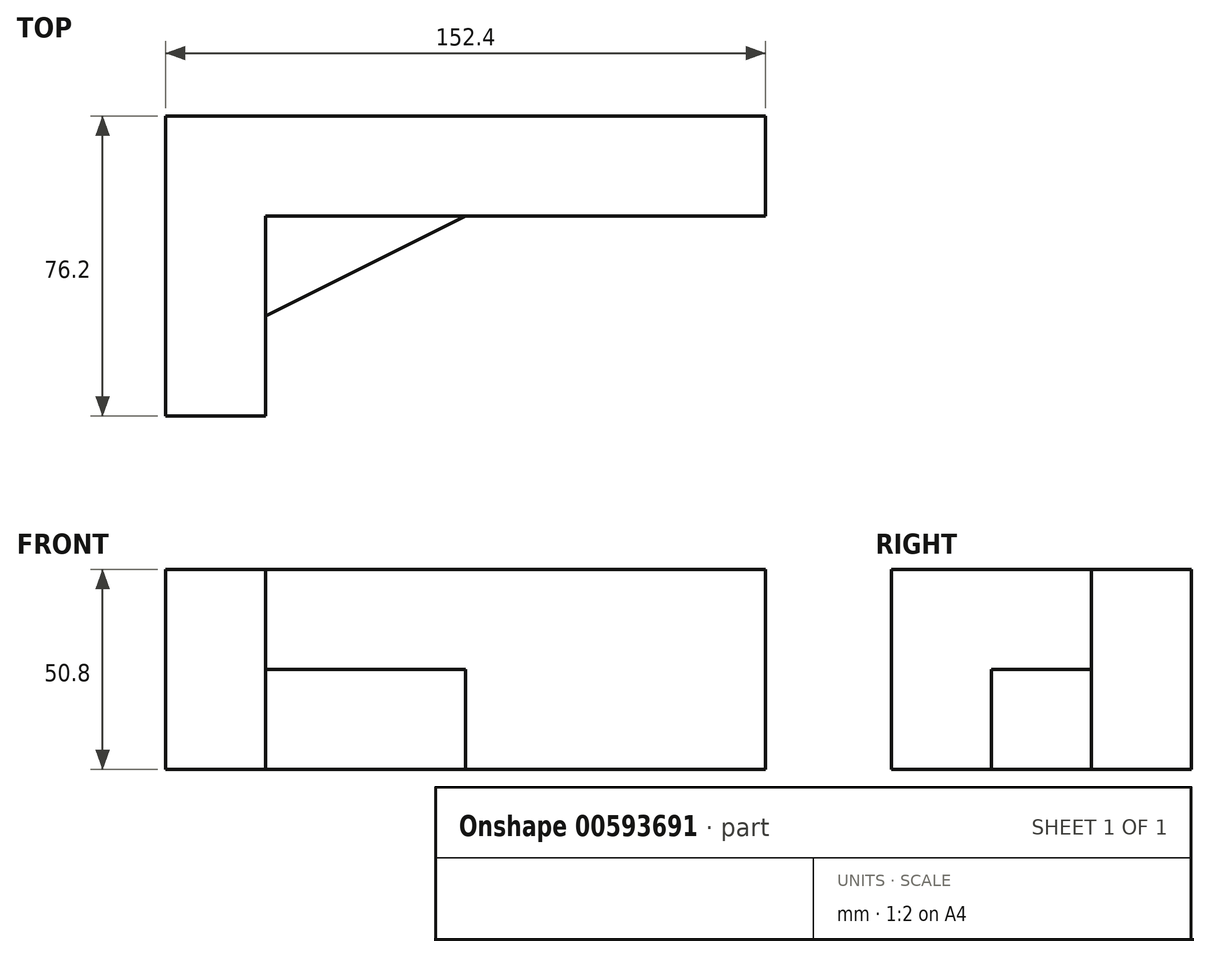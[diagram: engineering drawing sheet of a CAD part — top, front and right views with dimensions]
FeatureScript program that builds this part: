
annotation { "Feature Type Name" : "Feature", "Feature Type Description" : "" }
export const myFeature = defineFeature(function(context is Context, id is Id, definition is map)
    precondition{}
    {
        {
            var Q0;
            Q0=qCreatedBy(makeId("Front.planeOp"),FACE);
            var sketch = newSketch(context, id + "F0", { "sketchPlane" : qUnion([Q0])});
            skLineSegment(sketch, "E0", {"start": v(0, 0) * mm, "end": v(152.4, 0) * mm});
            skLineSegment(sketch, "E1", {"start": v(152.4, 0) * mm, "end": v(152.4, 50.8) * mm});
            skLineSegment(sketch, "E2", {"start": v(152.4, 50.8) * mm, "end": v(0, 50.8) * mm});
            skLineSegment(sketch, "E3", {"start": v(0, 50.8) * mm, "end": v(0, 0) * mm});
            skSolve(sketch);
        }
        {
            var Q0;
            Q0=makeQuery(id+"F0.imprint","IMPRINT",FACE,{"disambiguationData":[TD([[makeQuery(id+"F0.imprint","IMPRINT",EDGE,{"derivedFrom":sQuery(id+"F0.wireOp",EDGE,"E0")}),1.0]])]});
            extrude(context, id + "F1", {"entities" : qUnion([Q0]), "oppositeDirection" : true, "depth" : 76.2 * mm, "offsetDistance" : 25.4 * mm});
        }
        {
            var Q0;
            Q0=makeQuery(id+"F1.opExtrude","CAP_FACE",FACE,{"disambiguationData":[OSD([sQuery(id+"F0.wireOp",EDGE,"E0"),sQuery(id+"F0.wireOp",EDGE,"E1"),sQuery(id+"F0.wireOp",EDGE,"E2"),sQuery(id+"F0.wireOp",EDGE,"E3")])],"isStart":true});
            var sketch = newSketch(context, id + "F2", { "sketchPlane" : qUnion([Q0])});
            skLineSegment(sketch, "E4.bottom", {"start": v(152.4, 0) * mm, "end": v(25.4, 0) * mm});
            skLineSegment(sketch, "E4.top", {"start": v(152.4, 50.8) * mm, "end": v(25.4, 50.8) * mm});
            skLineSegment(sketch, "E4.left", {"start": v(152.4, 0) * mm, "end": v(152.4, 50.8) * mm});
            skLineSegment(sketch, "E4.right", {"start": v(25.4, 0) * mm, "end": v(25.4, 50.8) * mm});
            skSolve(sketch);
        }
        {
            var Q0;
            Q0=makeQuery(id+"F2.imprint","IMPRINT",FACE,{"disambiguationData":[TD([[makeQuery(id+"F2.imprint","IMPRINT",EDGE,{"derivedFrom":sQuery(id+"F2.wireOp",EDGE,"E4.bottom")}),1.0]])]});
            extrude(context, id + "F3", {"entities" : qUnion([Q0]), "operationType" : NewBodyOperationType.REMOVE, "oppositeDirection" : true, "depth" : 50.8 * mm, "offsetDistance" : 25.4 * mm});
        }
        {
            var Q0;
            Q0=makeQuery(id+"F3.boolean.opBoolean","COPY",FACE,{"derivedFrom":makeQuery(id+"F3.opExtrude","CAP_FACE",FACE,{"disambiguationData":[OSD([sQuery(id+"F2.wireOp",EDGE,"E4.bottom"),sQuery(id+"F2.wireOp",EDGE,"E4.top"),sQuery(id+"F2.wireOp",EDGE,"E4.left"),sQuery(id+"F2.wireOp",EDGE,"E4.right")])],"isStart":false})});
            var sketch = newSketch(context, id + "F4", { "sketchPlane" : qUnion([Q0])});
            skLineSegment(sketch, "E5.bottom", {"start": v(25.4, 0) * mm, "end": v(76.2, 0) * mm});
            skLineSegment(sketch, "E5.top", {"start": v(25.4, 25.4) * mm, "end": v(76.2, 25.4) * mm});
            skLineSegment(sketch, "E5.left", {"start": v(25.4, 0) * mm, "end": v(25.4, 25.4) * mm});
            skLineSegment(sketch, "E5.right", {"start": v(76.2, 0) * mm, "end": v(76.2, 25.4) * mm});
            skSolve(sketch);
        }
        {
            var Q0;
            Q0=makeQuery(id+"F4.imprint","IMPRINT",FACE,{"disambiguationData":[TD([[makeQuery(id+"F4.imprint","IMPRINT",EDGE,{"derivedFrom":sQuery(id+"F4.wireOp",EDGE,"E5.bottom")}),1.0]])]});
            extrude(context, id + "F5", {"entities" : qUnion([Q0]), "operationType" : NewBodyOperationType.ADD, "depth" : 25.4 * mm, "offsetDistance" : 25.4 * mm});
        }
        {
            var Q0;
            Q0=makeQuery(id+"F5.opExtrude","SWEPT_FACE",FACE,{"disambiguationData":[OSD([sQuery(id+"F4.wireOp",EDGE,"E5.top")])]});
            var sketch = newSketch(context, id + "F6", { "sketchPlane" : qUnion([Q0])});
            skLineSegment(sketch, "E6", {"start": v(25.4, 25.4) * mm, "end": v(76.2, 50.8) * mm});
            skSolve(sketch);
        }
        {
            var Q0;
            Q0=makeQuery(id+"F6.imprint","IMPRINT",FACE,{"disambiguationData":[TD([[makeQuery(id+"F6.imprint","IMPRINT",EDGE,{"derivedFrom":sQuery(id+"F6.wireOp",EDGE,"E6")}),-1.0]])]});
            extrude(context, id + "F7", {"entities" : qUnion([Q0]), "operationType" : NewBodyOperationType.REMOVE, "oppositeDirection" : true, "depth" : 25.4 * mm, "offsetDistance" : 25.4 * mm});
        }
    });
